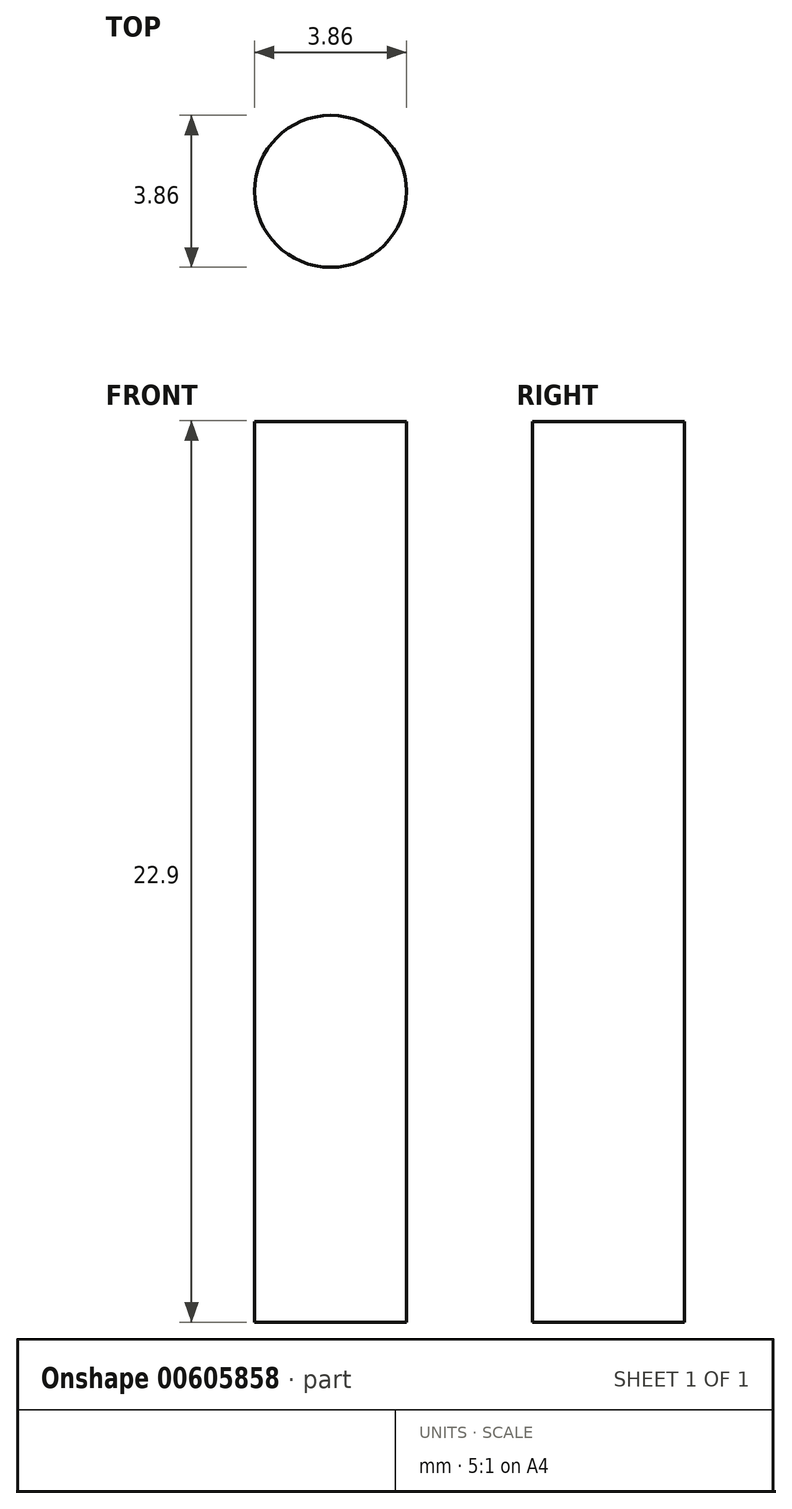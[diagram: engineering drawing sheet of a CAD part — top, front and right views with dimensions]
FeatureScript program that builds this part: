
annotation { "Feature Type Name" : "Feature", "Feature Type Description" : "" }
export const myFeature = defineFeature(function(context is Context, id is Id, definition is map)
    precondition{}
    {
        {
            var Q0;
            Q0=qCreatedBy(makeId("Front.planeOp"),FACE);
            var sketch = newSketch(context, id + "F0", { "sketchPlane" : qUnion([Q0])});
            skLineSegment(sketch, "E0", {"start": v(0, 0) * mm, "end": v(0, 22.9) * mm});
            skLineSegment(sketch, "E1", {"start": v(0, 0) * mm, "end": v(1.93, 0) * mm});
            skLineSegment(sketch, "E2", {"start": v(1.93, 0) * mm, "end": v(1.93, 22.88) * mm});
            skLineSegment(sketch, "E3", {"start": v(1.93, 22.88) * mm, "end": v(0, 22.9) * mm});
            skSolve(sketch);
        }
        {
            var Q0;
            Q0=makeQuery(id+"F0.imprint","IMPRINT",FACE,{"disambiguationData":[TD([[makeQuery(id+"F0.imprint","IMPRINT",EDGE,{"derivedFrom":sQuery(id+"F0.wireOp",EDGE,"E0")}),-1.0]])]});
            var Q1;
            Q1=sQuery(id+"F0.wireOp",EDGE,"E0");
            revolve(context, id + "F1", {"entities" : qUnion([Q0]), "axis" : qUnion([Q1]), "revolveType" : RevolveType.FULL});
        }
    });
